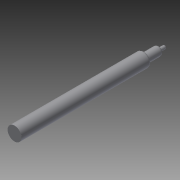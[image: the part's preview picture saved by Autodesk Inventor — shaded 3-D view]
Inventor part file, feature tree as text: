
AUTODESK INVENTOR PART (.ipt)
format: ipt  version: 2013 (Build 170138000, 138)  size: 92,160 bytes
history: native  units: mm
features: extrude x3, fillet x3, sketch x3
ambient origin geometry x8: Origin, YZ Plane, XZ Plane, XY Plane, X Axis, Y Axis, Z Axis, Center Point
bodies: Solid1 (feature_tree)
feature tree (9):
  extrude  "Extrusion1"  Depth=150.0mm TaperAngle=0.0deg
  extrude  "Extrusion2"  Depth=17.0mm TaperAngle=0.0deg
  extrude  "Extrusion3"  Depth=7.0mm TaperAngle=0.0deg
  fillet  "Fillet1"  Radius=3.0mm
  fillet  "Fillet2"  Radius=3.0mm
  fillet  "Fillet3"  Radius=2.0mm
  sketch  "Sketch1"  dims[d0=16.0mm d1=150.0mm d2=0.0mm]
  sketch  "Sketch2"  dims[d3=10.0mm d4=17.0mm d5=0.0mm]
  sketch  "Sketch3"  dims[d6=4.0mm d7=7.0mm d8=0.0mm d9=3.0mm d10=3.0mm d11=2.0mm]
